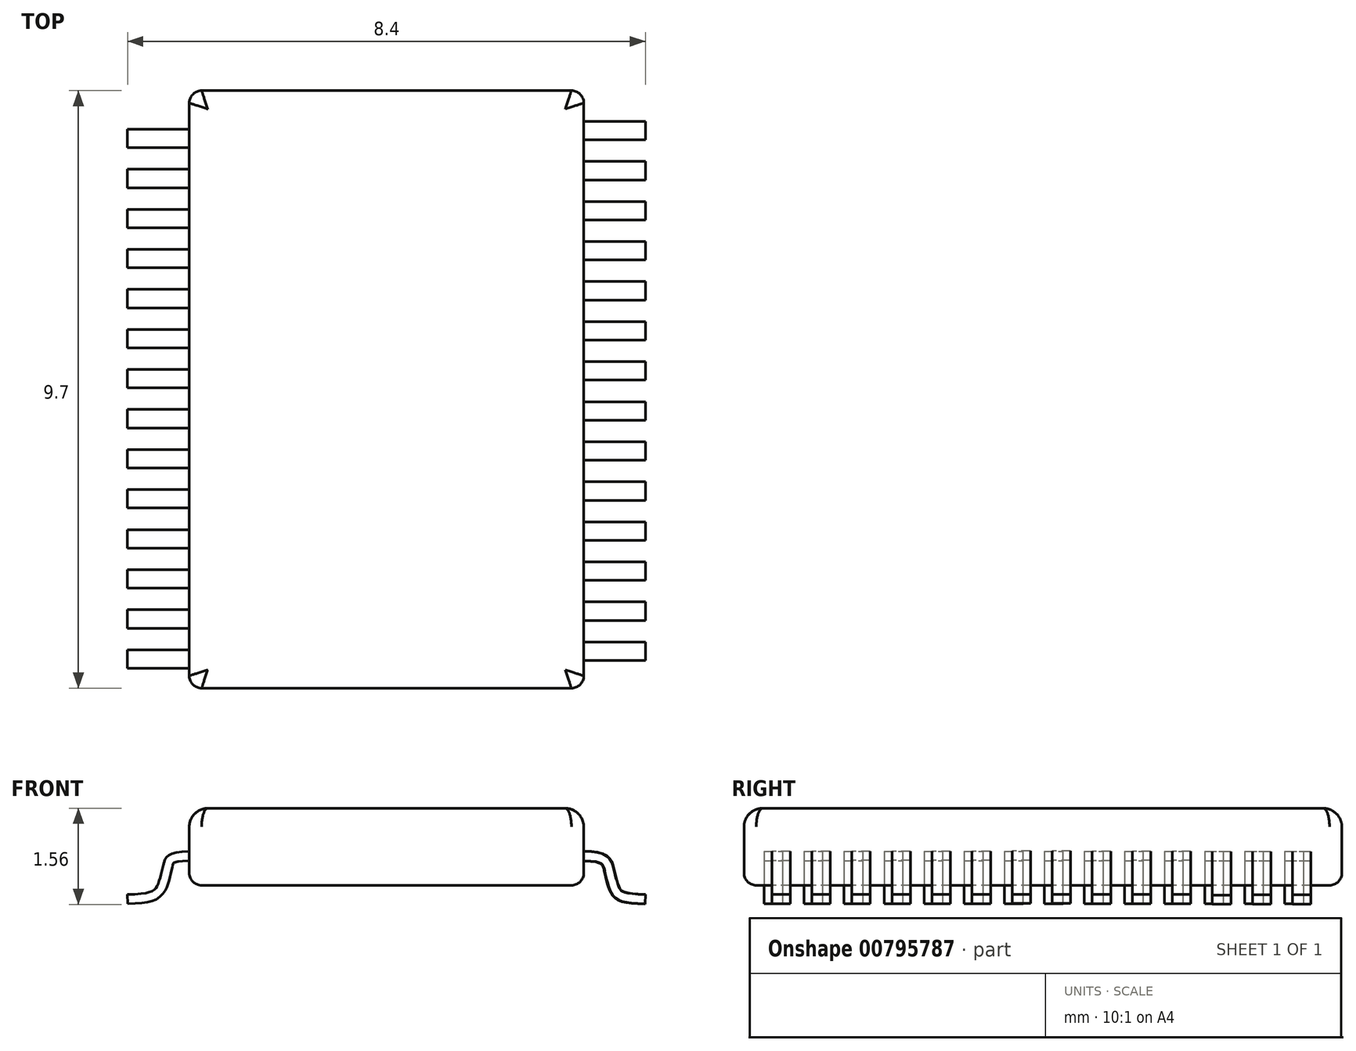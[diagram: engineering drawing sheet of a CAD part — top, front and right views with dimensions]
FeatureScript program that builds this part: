
annotation { "Feature Type Name" : "Feature", "Feature Type Description" : "" }
export const myFeature = defineFeature(function(context is Context, id is Id, definition is map)
    precondition{}
    {
        {
            var Q0;
            Q0=qCreatedBy(makeId("Top.planeOp"),FACE);
            var sketch = newSketch(context, id + "F0", { "sketchPlane" : qUnion([Q0])});
            skLineSegment(sketch, "E0.bottom", {"start": v(3.2, 4.85) * mm, "end": v(-3.2, 4.85) * mm});
            skLineSegment(sketch, "E0.top", {"start": v(3.2, -4.85) * mm, "end": v(-3.2, -4.85) * mm});
            skLineSegment(sketch, "E0.left", {"start": v(3.2, 4.85) * mm, "end": v(3.2, -4.85) * mm});
            skLineSegment(sketch, "E0.right", {"start": v(-3.2, 4.85) * mm, "end": v(-3.2, -4.85) * mm});
            skPoint(sketch, "E0.middle", {"position": v(0, 0) * mm});
            skSolve(sketch);
        }
        {
            var Q0;
            Q0 = qSketchRegion(id + "F0", true);
            extrude(context, id + "F1", {"entities" : qUnion([Q0]), "depth" : 1.25 * mm, "offsetDistance" : 25 * mm});
        }
        {
            var Q0;
            Q0=makeQuery(id+"F1.opExtrude","CAP_FACE",FACE,{"disambiguationData":[OSD([sQuery(id+"F0.wireOp",EDGE,"E0.bottom"),sQuery(id+"F0.wireOp",EDGE,"E0.top"),sQuery(id+"F0.wireOp",EDGE,"E0.left"),sQuery(id+"F0.wireOp",EDGE,"E0.right")])],"isStart":false});
            fillet(context, id + "F2", {"entities" : qUnion([Q0]), "radius" : 0.3 * mm, "tangentPropagation" : true, "allowEdgeOverflow" : false});
        }
        {
            var Q0;
            Q0=makeQuery(id+"F1.opExtrude","SWEPT_EDGE",EDGE,{"disambiguationData":[OSD([sQuery(id+"F0.wireOp",EDGE,"E0.bottom"),sQuery(id+"F0.wireOp",EDGE,"E0.right")])]});
            var Q1;
            Q1=makeQuery(id+"F1.opExtrude","SWEPT_EDGE",EDGE,{"disambiguationData":[OSD([sQuery(id+"F0.wireOp",EDGE,"E0.top"),sQuery(id+"F0.wireOp",EDGE,"E0.right")])]});
            var Q2;
            Q2=makeQuery(id+"F1.opExtrude","SWEPT_EDGE",EDGE,{"disambiguationData":[OSD([sQuery(id+"F0.wireOp",EDGE,"E0.top"),sQuery(id+"F0.wireOp",EDGE,"E0.left")])]});
            var Q3;
            Q3=makeQuery(id+"F1.opExtrude","SWEPT_EDGE",EDGE,{"disambiguationData":[OSD([sQuery(id+"F0.wireOp",EDGE,"E0.bottom"),sQuery(id+"F0.wireOp",EDGE,"E0.left")])]});
            fillet(context, id + "F3", {"entities" : qUnion([Q0, Q1, Q2, Q3]), "radius" : 0.2 * mm, "tangentPropagation" : true, "allowEdgeOverflow" : false});
        }
        {
            var Q0;
            Q0=makeQuery(id+"F1.opExtrude","CAP_FACE",FACE,{"disambiguationData":[OSD([sQuery(id+"F0.wireOp",EDGE,"E0.bottom"),sQuery(id+"F0.wireOp",EDGE,"E0.top"),sQuery(id+"F0.wireOp",EDGE,"E0.left"),sQuery(id+"F0.wireOp",EDGE,"E0.right")])],"isStart":true});
            fillet(context, id + "F4", {"entities" : qUnion([Q0]), "radius" : 0.2 * mm, "tangentPropagation" : true, "allowEdgeOverflow" : false});
        }
        {
            var Q0;
            Q0=makeQuery(id+"F1.opExtrude","SWEPT_FACE",FACE,{"disambiguationData":[OSD([sQuery(id+"F0.wireOp",EDGE,"E0.left")])]});
            var sketch = newSketch(context, id + "F5", { "sketchPlane" : qUnion([Q0])});
            skPoint(sketch, "E1.endSnap0", {"position": v(4.65, 0.57) * mm});
            skLineSegment(sketch, "E2.bottom", {"start": v(-4.1, 0.55) * mm, "end": v(-4.4, 0.55) * mm});
            skLineSegment(sketch, "E2.top", {"start": v(-4.1, 0.4) * mm, "end": v(-4.4, 0.4) * mm});
            skLineSegment(sketch, "E2.left", {"start": v(-4.1, 0.55) * mm, "end": v(-4.1, 0.4) * mm});
            skLineSegment(sketch, "E2.right", {"start": v(-4.4, 0.55) * mm, "end": v(-4.4, 0.4) * mm});
            skPoint(sketch, "E2.middle", {"position": v(-4.25, 0.48) * mm});
            skLineSegment(sketch, "E3.bottom", {"start": v(-3.45, 0.55) * mm, "end": v(-3.75, 0.55) * mm});
            skLineSegment(sketch, "E3.top", {"start": v(-3.45, 0.4) * mm, "end": v(-3.75, 0.4) * mm});
            skLineSegment(sketch, "E3.left", {"start": v(-3.45, 0.55) * mm, "end": v(-3.45, 0.4) * mm});
            skLineSegment(sketch, "E3.right", {"start": v(-3.75, 0.55) * mm, "end": v(-3.75, 0.4) * mm});
            skPoint(sketch, "E3.middle", {"position": v(-3.6, 0.48) * mm});
            skLineSegment(sketch, "E4.bottom", {"start": v(-2.8, 0.55) * mm, "end": v(-3.1, 0.55) * mm});
            skLineSegment(sketch, "E4.top", {"start": v(-2.8, 0.4) * mm, "end": v(-3.1, 0.4) * mm});
            skLineSegment(sketch, "E4.left", {"start": v(-2.8, 0.55) * mm, "end": v(-2.8, 0.4) * mm});
            skLineSegment(sketch, "E4.right", {"start": v(-3.1, 0.55) * mm, "end": v(-3.1, 0.4) * mm});
            skPoint(sketch, "E4.middle", {"position": v(-2.95, 0.48) * mm});
            skPoint(sketch, "E5.middle", {"position": v(-1.27, 0.47) * mm});
            skLineSegment(sketch, "E6.bottom", {"start": v(-2.15, 0.55) * mm, "end": v(-2.45, 0.55) * mm});
            skLineSegment(sketch, "E6.top", {"start": v(-2.15, 0.4) * mm, "end": v(-2.45, 0.4) * mm});
            skLineSegment(sketch, "E6.left", {"start": v(-2.15, 0.55) * mm, "end": v(-2.15, 0.4) * mm});
            skLineSegment(sketch, "E6.right", {"start": v(-2.45, 0.55) * mm, "end": v(-2.45, 0.4) * mm});
            skPoint(sketch, "E6.middle", {"position": v(-2.3, 0.48) * mm});
            skLineSegment(sketch, "E7.bottom", {"start": v(-1.5, 0.55) * mm, "end": v(-1.8, 0.55) * mm});
            skLineSegment(sketch, "E7.top", {"start": v(-1.5, 0.4) * mm, "end": v(-1.8, 0.4) * mm});
            skLineSegment(sketch, "E7.left", {"start": v(-1.5, 0.55) * mm, "end": v(-1.5, 0.4) * mm});
            skLineSegment(sketch, "E7.right", {"start": v(-1.8, 0.55) * mm, "end": v(-1.8, 0.4) * mm});
            skLineSegment(sketch, "E8.bottom", {"start": v(-0.85, 0.55) * mm, "end": v(-1.15, 0.55) * mm});
            skLineSegment(sketch, "E8.top", {"start": v(-0.85, 0.4) * mm, "end": v(-1.15, 0.4) * mm});
            skLineSegment(sketch, "E8.left", {"start": v(-0.85, 0.55) * mm, "end": v(-0.85, 0.4) * mm});
            skLineSegment(sketch, "E8.right", {"start": v(-1.15, 0.55) * mm, "end": v(-1.15, 0.4) * mm});
            skLineSegment(sketch, "E9.bottom", {"start": v(-0.2, 0.55) * mm, "end": v(-0.5, 0.55) * mm});
            skLineSegment(sketch, "E9.top", {"start": v(-0.2, 0.4) * mm, "end": v(-0.5, 0.4) * mm});
            skLineSegment(sketch, "E9.left", {"start": v(-0.2, 0.55) * mm, "end": v(-0.2, 0.4) * mm});
            skLineSegment(sketch, "E9.right", {"start": v(-0.5, 0.55) * mm, "end": v(-0.5, 0.4) * mm});
            skLineSegment(sketch, "E10.bottom", {"start": v(0.45, 0.55) * mm, "end": v(0.15, 0.55) * mm});
            skLineSegment(sketch, "E10.top", {"start": v(0.45, 0.4) * mm, "end": v(0.15, 0.4) * mm});
            skLineSegment(sketch, "E10.left", {"start": v(0.45, 0.55) * mm, "end": v(0.45, 0.4) * mm});
            skLineSegment(sketch, "E10.right", {"start": v(0.15, 0.55) * mm, "end": v(0.15, 0.4) * mm});
            skLineSegment(sketch, "E11.bottom", {"start": v(1.1, 0.55) * mm, "end": v(0.8, 0.55) * mm});
            skLineSegment(sketch, "E11.top", {"start": v(1.1, 0.4) * mm, "end": v(0.8, 0.4) * mm});
            skLineSegment(sketch, "E11.left", {"start": v(1.1, 0.55) * mm, "end": v(1.1, 0.4) * mm});
            skLineSegment(sketch, "E11.right", {"start": v(0.8, 0.55) * mm, "end": v(0.8, 0.4) * mm});
            skLineSegment(sketch, "E12.bottom", {"start": v(1.75, 0.55) * mm, "end": v(1.45, 0.55) * mm});
            skLineSegment(sketch, "E12.top", {"start": v(1.75, 0.4) * mm, "end": v(1.45, 0.4) * mm});
            skLineSegment(sketch, "E12.left", {"start": v(1.75, 0.55) * mm, "end": v(1.75, 0.4) * mm});
            skLineSegment(sketch, "E12.right", {"start": v(1.45, 0.55) * mm, "end": v(1.45, 0.4) * mm});
            skLineSegment(sketch, "E13.bottom", {"start": v(2.4, 0.55) * mm, "end": v(2.1, 0.55) * mm});
            skLineSegment(sketch, "E13.top", {"start": v(2.4, 0.4) * mm, "end": v(2.1, 0.4) * mm});
            skLineSegment(sketch, "E13.left", {"start": v(2.4, 0.55) * mm, "end": v(2.4, 0.4) * mm});
            skLineSegment(sketch, "E13.right", {"start": v(2.1, 0.55) * mm, "end": v(2.1, 0.4) * mm});
            skLineSegment(sketch, "E14.bottom", {"start": v(3.05, 0.54) * mm, "end": v(2.75, 0.54) * mm});
            skLineSegment(sketch, "E14.top", {"start": v(3.05, 0.4) * mm, "end": v(2.75, 0.4) * mm});
            skLineSegment(sketch, "E14.left", {"start": v(3.05, 0.54) * mm, "end": v(3.05, 0.4) * mm});
            skLineSegment(sketch, "E14.right", {"start": v(2.75, 0.54) * mm, "end": v(2.75, 0.4) * mm});
            skLineSegment(sketch, "E15.bottom", {"start": v(3.7, 0.54) * mm, "end": v(3.4, 0.54) * mm});
            skLineSegment(sketch, "E15.top", {"start": v(3.7, 0.4) * mm, "end": v(3.4, 0.4) * mm});
            skLineSegment(sketch, "E15.left", {"start": v(3.7, 0.54) * mm, "end": v(3.7, 0.4) * mm});
            skLineSegment(sketch, "E15.right", {"start": v(3.4, 0.54) * mm, "end": v(3.4, 0.4) * mm});
            skLineSegment(sketch, "E16.bottom", {"start": v(4.35, 0.54) * mm, "end": v(4.05, 0.54) * mm});
            skLineSegment(sketch, "E16.top", {"start": v(4.35, 0.4) * mm, "end": v(4.05, 0.4) * mm});
            skLineSegment(sketch, "E16.left", {"start": v(4.35, 0.54) * mm, "end": v(4.35, 0.4) * mm});
            skLineSegment(sketch, "E16.right", {"start": v(4.05, 0.54) * mm, "end": v(4.05, 0.4) * mm});
            skLineSegment(sketch, "E17", {"start": v(-4.65, 0.57) * mm, "end": v(4.65, 0.57) * mm, "construction": true});
            skSolve(sketch);
        }
        {
            var Q0;
            Q0=makeQuery(id+"F1.opExtrude","SWEPT_FACE",FACE,{"disambiguationData":[OSD([sQuery(id+"F0.wireOp",EDGE,"E0.bottom")])]});
            var sketch = newSketch(context, id + "F6", { "sketchPlane" : qUnion([Q0])});
            skFitSpline(sketch, "E18", {"points": [v(-3.2, 0.47) * mm, v(-3.6, 0.27) * mm, v(-3.7, -0.07) * mm, v(-4.2, -0.23) * mm], "startDerivative": vector(-3.06, -0.02) * mm, "endDerivative": vector(-3.04, -0.08) * mm});
            skFitSpline(sketch, "E19.MirrorCS", {"points": [v(3.2, 0.54) * mm, v(3.6, 0.34) * mm, v(3.7, 0) * mm, v(4.2, -0.16) * mm], "startDerivative": vector(3.06, -0.02) * mm, "endDerivative": vector(3.04, -0.08) * mm});
            skFitSpline(sketch, "E20.MirrorCS", {"points": [v(3.2, 0.54) * mm, v(3.6, 0.34) * mm, v(3.7, 0) * mm, v(4.2, -0.16) * mm], "startDerivative": vector(3.06, -0.02) * mm, "endDerivative": vector(3.04, -0.08) * mm});
            skSolve(sketch);
        }
        {
            var Q0;
            Q0=makeQuery(id+"F5.imprint","IMPRINT",FACE,{"disambiguationData":[TD([[makeQuery(id+"F5.imprint","IMPRINT",EDGE,{"derivedFrom":sQuery(id+"F5.wireOp",EDGE,"E16.bottom")}),1.0]])]});
            var Q1;
            Q1=makeQuery(id+"F5.imprint","IMPRINT",FACE,{"disambiguationData":[TD([[makeQuery(id+"F5.imprint","IMPRINT",EDGE,{"derivedFrom":sQuery(id+"F5.wireOp",EDGE,"E15.bottom")}),1.0]])]});
            var Q2;
            Q2=makeQuery(id+"F5.imprint","IMPRINT",FACE,{"disambiguationData":[TD([[makeQuery(id+"F5.imprint","IMPRINT",EDGE,{"derivedFrom":sQuery(id+"F5.wireOp",EDGE,"E14.bottom")}),1.0]])]});
            var Q3;
            Q3=makeQuery(id+"F5.imprint","IMPRINT",FACE,{"disambiguationData":[TD([[makeQuery(id+"F5.imprint","IMPRINT",EDGE,{"derivedFrom":sQuery(id+"F5.wireOp",EDGE,"E13.bottom")}),1.0]])]});
            var Q4;
            Q4=makeQuery(id+"F5.imprint","IMPRINT",FACE,{"disambiguationData":[TD([[makeQuery(id+"F5.imprint","IMPRINT",EDGE,{"derivedFrom":sQuery(id+"F5.wireOp",EDGE,"E12.bottom")}),1.0]])]});
            var Q5;
            Q5=makeQuery(id+"F5.imprint","IMPRINT",FACE,{"disambiguationData":[TD([[makeQuery(id+"F5.imprint","IMPRINT",EDGE,{"derivedFrom":sQuery(id+"F5.wireOp",EDGE,"E11.bottom")}),1.0]])]});
            var Q6;
            Q6=makeQuery(id+"F5.imprint","IMPRINT",FACE,{"disambiguationData":[TD([[makeQuery(id+"F5.imprint","IMPRINT",EDGE,{"derivedFrom":sQuery(id+"F5.wireOp",EDGE,"E10.bottom")}),1.0]])]});
            var Q7;
            Q7=makeQuery(id+"F5.imprint","IMPRINT",FACE,{"disambiguationData":[TD([[makeQuery(id+"F5.imprint","IMPRINT",EDGE,{"derivedFrom":sQuery(id+"F5.wireOp",EDGE,"E9.bottom")}),1.0]])]});
            var Q8;
            Q8=makeQuery(id+"F5.imprint","IMPRINT",FACE,{"disambiguationData":[TD([[makeQuery(id+"F5.imprint","IMPRINT",EDGE,{"derivedFrom":sQuery(id+"F5.wireOp",EDGE,"E8.bottom")}),1.0]])]});
            var Q9;
            Q9=makeQuery(id+"F5.imprint","IMPRINT",FACE,{"disambiguationData":[TD([[makeQuery(id+"F5.imprint","IMPRINT",EDGE,{"derivedFrom":sQuery(id+"F5.wireOp",EDGE,"E7.bottom")}),1.0]])]});
            var Q10;
            Q10=makeQuery(id+"F5.imprint","IMPRINT",FACE,{"disambiguationData":[TD([[makeQuery(id+"F5.imprint","IMPRINT",EDGE,{"derivedFrom":sQuery(id+"F5.wireOp",EDGE,"E6.bottom")}),1.0]])]});
            var Q11;
            Q11=makeQuery(id+"F5.imprint","IMPRINT",FACE,{"disambiguationData":[TD([[makeQuery(id+"F5.imprint","IMPRINT",EDGE,{"derivedFrom":sQuery(id+"F5.wireOp",EDGE,"E4.bottom")}),1.0]])]});
            var Q12;
            Q12=makeQuery(id+"F5.imprint","IMPRINT",FACE,{"disambiguationData":[TD([[makeQuery(id+"F5.imprint","IMPRINT",EDGE,{"derivedFrom":sQuery(id+"F5.wireOp",EDGE,"E3.bottom")}),1.0]])]});
            var Q13;
            Q13=makeQuery(id+"F5.imprint","IMPRINT",FACE,{"disambiguationData":[TD([[makeQuery(id+"F5.imprint","IMPRINT",EDGE,{"derivedFrom":sQuery(id+"F5.wireOp",EDGE,"E2.bottom")}),1.0]])]});
            var Q14;
            Q14=sQuery(id+"F6.wireOp",EDGE,"E18");
            sweep(context, id + "F7", {"profiles" : qUnion([Q0, Q1, Q2, Q3, Q4, Q5, Q6, Q7, Q8, Q9, Q10, Q11, Q12, Q13]), "path" : qUnion([Q14])});
        }
        {
            var Q0;
            Q0=makeQuery(id+"F1.opExtrude","SWEPT_FACE",FACE,{"disambiguationData":[OSD([sQuery(id+"F0.wireOp",EDGE,"E0.right")])]});
            var sketch = newSketch(context, id + "F8", { "sketchPlane" : qUnion([Q0])});
            skPoint(sketch, "E21.endSnap0", {"position": v(4.83, 0.67) * mm});
            skLineSegment(sketch, "E22.bottom", {"start": v(-3.92, 0.55) * mm, "end": v(-4.22, 0.55) * mm});
            skLineSegment(sketch, "E22.top", {"start": v(-3.92, 0.4) * mm, "end": v(-4.22, 0.4) * mm});
            skLineSegment(sketch, "E22.left", {"start": v(-3.92, 0.55) * mm, "end": v(-3.92, 0.4) * mm});
            skLineSegment(sketch, "E22.right", {"start": v(-4.22, 0.55) * mm, "end": v(-4.22, 0.4) * mm});
            skPoint(sketch, "E22.middle", {"position": v(-4.07, 0.48) * mm});
            skLineSegment(sketch, "E23.bottom", {"start": v(-3.27, 0.55) * mm, "end": v(-3.57, 0.55) * mm});
            skLineSegment(sketch, "E23.top", {"start": v(-3.27, 0.4) * mm, "end": v(-3.57, 0.4) * mm});
            skLineSegment(sketch, "E23.left", {"start": v(-3.27, 0.55) * mm, "end": v(-3.27, 0.4) * mm});
            skLineSegment(sketch, "E23.right", {"start": v(-3.57, 0.55) * mm, "end": v(-3.57, 0.4) * mm});
            skPoint(sketch, "E23.middle", {"position": v(-3.42, 0.47) * mm});
            skLineSegment(sketch, "E24.bottom", {"start": v(-2.62, 0.55) * mm, "end": v(-2.92, 0.55) * mm});
            skLineSegment(sketch, "E24.top", {"start": v(-2.62, 0.4) * mm, "end": v(-2.92, 0.4) * mm});
            skLineSegment(sketch, "E24.left", {"start": v(-2.62, 0.55) * mm, "end": v(-2.62, 0.4) * mm});
            skLineSegment(sketch, "E24.right", {"start": v(-2.92, 0.55) * mm, "end": v(-2.92, 0.4) * mm});
            skPoint(sketch, "E24.middle", {"position": v(-2.77, 0.47) * mm});
            skPoint(sketch, "E25.middle", {"position": v(-1.1, 0.57) * mm});
            skLineSegment(sketch, "E26.bottom", {"start": v(-1.97, 0.55) * mm, "end": v(-2.27, 0.55) * mm});
            skLineSegment(sketch, "E26.top", {"start": v(-1.97, 0.4) * mm, "end": v(-2.27, 0.4) * mm});
            skLineSegment(sketch, "E26.left", {"start": v(-1.97, 0.55) * mm, "end": v(-1.97, 0.4) * mm});
            skLineSegment(sketch, "E26.right", {"start": v(-2.27, 0.55) * mm, "end": v(-2.27, 0.4) * mm});
            skPoint(sketch, "E26.middle", {"position": v(-2.12, 0.47) * mm});
            skLineSegment(sketch, "E27.bottom", {"start": v(-1.32, 0.55) * mm, "end": v(-1.62, 0.55) * mm});
            skLineSegment(sketch, "E27.top", {"start": v(-1.32, 0.4) * mm, "end": v(-1.62, 0.4) * mm});
            skLineSegment(sketch, "E27.left", {"start": v(-1.32, 0.55) * mm, "end": v(-1.32, 0.4) * mm});
            skLineSegment(sketch, "E27.right", {"start": v(-1.62, 0.55) * mm, "end": v(-1.62, 0.4) * mm});
            skLineSegment(sketch, "E28.bottom", {"start": v(-0.67, 0.55) * mm, "end": v(-0.97, 0.55) * mm});
            skLineSegment(sketch, "E28.top", {"start": v(-0.67, 0.4) * mm, "end": v(-0.97, 0.4) * mm});
            skLineSegment(sketch, "E28.left", {"start": v(-0.67, 0.55) * mm, "end": v(-0.67, 0.4) * mm});
            skLineSegment(sketch, "E28.right", {"start": v(-0.97, 0.55) * mm, "end": v(-0.97, 0.4) * mm});
            skLineSegment(sketch, "E29.bottom", {"start": v(-0.02, 0.55) * mm, "end": v(-0.32, 0.55) * mm});
            skLineSegment(sketch, "E29.top", {"start": v(-0.02, 0.4) * mm, "end": v(-0.32, 0.4) * mm});
            skLineSegment(sketch, "E29.left", {"start": v(-0.02, 0.55) * mm, "end": v(-0.02, 0.4) * mm});
            skLineSegment(sketch, "E29.right", {"start": v(-0.32, 0.55) * mm, "end": v(-0.32, 0.4) * mm});
            skLineSegment(sketch, "E30.bottom", {"start": v(0.63, 0.55) * mm, "end": v(0.33, 0.55) * mm});
            skLineSegment(sketch, "E30.top", {"start": v(0.63, 0.4) * mm, "end": v(0.33, 0.4) * mm});
            skLineSegment(sketch, "E30.left", {"start": v(0.63, 0.55) * mm, "end": v(0.63, 0.4) * mm});
            skLineSegment(sketch, "E30.right", {"start": v(0.33, 0.55) * mm, "end": v(0.33, 0.4) * mm});
            skLineSegment(sketch, "E31.bottom", {"start": v(1.28, 0.55) * mm, "end": v(0.98, 0.55) * mm});
            skLineSegment(sketch, "E31.top", {"start": v(1.28, 0.4) * mm, "end": v(0.98, 0.4) * mm});
            skLineSegment(sketch, "E31.left", {"start": v(1.28, 0.55) * mm, "end": v(1.28, 0.4) * mm});
            skLineSegment(sketch, "E31.right", {"start": v(0.98, 0.55) * mm, "end": v(0.98, 0.4) * mm});
            skLineSegment(sketch, "E32.bottom", {"start": v(1.93, 0.55) * mm, "end": v(1.63, 0.55) * mm});
            skLineSegment(sketch, "E32.top", {"start": v(1.93, 0.4) * mm, "end": v(1.63, 0.4) * mm});
            skLineSegment(sketch, "E32.left", {"start": v(1.93, 0.55) * mm, "end": v(1.93, 0.4) * mm});
            skLineSegment(sketch, "E32.right", {"start": v(1.63, 0.55) * mm, "end": v(1.63, 0.4) * mm});
            skLineSegment(sketch, "E33.bottom", {"start": v(2.58, 0.55) * mm, "end": v(2.28, 0.55) * mm});
            skLineSegment(sketch, "E33.top", {"start": v(2.58, 0.4) * mm, "end": v(2.28, 0.4) * mm});
            skLineSegment(sketch, "E33.left", {"start": v(2.58, 0.55) * mm, "end": v(2.58, 0.4) * mm});
            skLineSegment(sketch, "E33.right", {"start": v(2.28, 0.55) * mm, "end": v(2.28, 0.4) * mm});
            skLineSegment(sketch, "E34.bottom", {"start": v(3.23, 0.55) * mm, "end": v(2.93, 0.55) * mm});
            skLineSegment(sketch, "E34.top", {"start": v(3.23, 0.4) * mm, "end": v(2.93, 0.4) * mm});
            skLineSegment(sketch, "E34.left", {"start": v(3.23, 0.55) * mm, "end": v(3.23, 0.4) * mm});
            skLineSegment(sketch, "E34.right", {"start": v(2.93, 0.55) * mm, "end": v(2.93, 0.4) * mm});
            skLineSegment(sketch, "E35.bottom", {"start": v(3.88, 0.55) * mm, "end": v(3.58, 0.55) * mm});
            skLineSegment(sketch, "E35.top", {"start": v(3.88, 0.4) * mm, "end": v(3.58, 0.4) * mm});
            skLineSegment(sketch, "E35.left", {"start": v(3.88, 0.55) * mm, "end": v(3.88, 0.4) * mm});
            skLineSegment(sketch, "E35.right", {"start": v(3.58, 0.55) * mm, "end": v(3.58, 0.4) * mm});
            skLineSegment(sketch, "E36.bottom", {"start": v(4.53, 0.55) * mm, "end": v(4.23, 0.55) * mm});
            skLineSegment(sketch, "E36.top", {"start": v(4.53, 0.4) * mm, "end": v(4.23, 0.4) * mm});
            skLineSegment(sketch, "E36.left", {"start": v(4.53, 0.55) * mm, "end": v(4.53, 0.4) * mm});
            skLineSegment(sketch, "E36.right", {"start": v(4.23, 0.55) * mm, "end": v(4.23, 0.4) * mm});
            skSolve(sketch);
        }
        {
            var Q0;
            Q0=makeQuery(id+"F8.imprint","IMPRINT",FACE,{"disambiguationData":[TD([[makeQuery(id+"F8.imprint","IMPRINT",EDGE,{"derivedFrom":sQuery(id+"F8.wireOp",EDGE,"E22.bottom")}),1.0]])]});
            var Q1;
            Q1=makeQuery(id+"F8.imprint","IMPRINT",FACE,{"disambiguationData":[TD([[makeQuery(id+"F8.imprint","IMPRINT",EDGE,{"derivedFrom":sQuery(id+"F8.wireOp",EDGE,"E23.bottom")}),1.0]])]});
            var Q2;
            Q2=makeQuery(id+"F8.imprint","IMPRINT",FACE,{"disambiguationData":[TD([[makeQuery(id+"F8.imprint","IMPRINT",EDGE,{"derivedFrom":sQuery(id+"F8.wireOp",EDGE,"E24.bottom")}),1.0]])]});
            var Q3;
            Q3=makeQuery(id+"F8.imprint","IMPRINT",FACE,{"disambiguationData":[TD([[makeQuery(id+"F8.imprint","IMPRINT",EDGE,{"derivedFrom":sQuery(id+"F8.wireOp",EDGE,"E26.bottom")}),1.0]])]});
            var Q4;
            Q4=makeQuery(id+"F8.imprint","IMPRINT",FACE,{"disambiguationData":[TD([[makeQuery(id+"F8.imprint","IMPRINT",EDGE,{"derivedFrom":sQuery(id+"F8.wireOp",EDGE,"E27.bottom")}),1.0]])]});
            var Q5;
            Q5=makeQuery(id+"F8.imprint","IMPRINT",FACE,{"disambiguationData":[TD([[makeQuery(id+"F8.imprint","IMPRINT",EDGE,{"derivedFrom":sQuery(id+"F8.wireOp",EDGE,"E28.bottom")}),1.0]])]});
            var Q6;
            Q6=makeQuery(id+"F8.imprint","IMPRINT",FACE,{"disambiguationData":[TD([[makeQuery(id+"F8.imprint","IMPRINT",EDGE,{"derivedFrom":sQuery(id+"F8.wireOp",EDGE,"E29.bottom")}),1.0]])]});
            var Q7;
            Q7=makeQuery(id+"F8.imprint","IMPRINT",FACE,{"disambiguationData":[TD([[makeQuery(id+"F8.imprint","IMPRINT",EDGE,{"derivedFrom":sQuery(id+"F8.wireOp",EDGE,"E30.bottom")}),1.0]])]});
            var Q8;
            Q8=makeQuery(id+"F8.imprint","IMPRINT",FACE,{"disambiguationData":[TD([[makeQuery(id+"F8.imprint","IMPRINT",EDGE,{"derivedFrom":sQuery(id+"F8.wireOp",EDGE,"E31.bottom")}),1.0]])]});
            var Q9;
            Q9=makeQuery(id+"F8.imprint","IMPRINT",FACE,{"disambiguationData":[TD([[makeQuery(id+"F8.imprint","IMPRINT",EDGE,{"derivedFrom":sQuery(id+"F8.wireOp",EDGE,"E32.bottom")}),1.0]])]});
            var Q10;
            Q10=makeQuery(id+"F8.imprint","IMPRINT",FACE,{"disambiguationData":[TD([[makeQuery(id+"F8.imprint","IMPRINT",EDGE,{"derivedFrom":sQuery(id+"F8.wireOp",EDGE,"E33.bottom")}),1.0]])]});
            var Q11;
            Q11=makeQuery(id+"F8.imprint","IMPRINT",FACE,{"disambiguationData":[TD([[makeQuery(id+"F8.imprint","IMPRINT",EDGE,{"derivedFrom":sQuery(id+"F8.wireOp",EDGE,"E34.bottom")}),1.0]])]});
            var Q12;
            Q12=makeQuery(id+"F8.imprint","IMPRINT",FACE,{"disambiguationData":[TD([[makeQuery(id+"F8.imprint","IMPRINT",EDGE,{"derivedFrom":sQuery(id+"F8.wireOp",EDGE,"E35.bottom")}),1.0]])]});
            var Q13;
            Q13=makeQuery(id+"F8.imprint","IMPRINT",FACE,{"disambiguationData":[TD([[makeQuery(id+"F8.imprint","IMPRINT",EDGE,{"derivedFrom":sQuery(id+"F8.wireOp",EDGE,"E36.bottom")}),1.0]])]});
            var Q14;
            Q14=sQuery(id+"F6.wireOp",EDGE,"E20.MirrorCS");
            sweep(context, id + "F9", {"profiles" : qUnion([Q0, Q1, Q2, Q3, Q4, Q5, Q6, Q7, Q8, Q9, Q10, Q11, Q12, Q13]), "path" : qUnion([Q14])});
        }
    });
